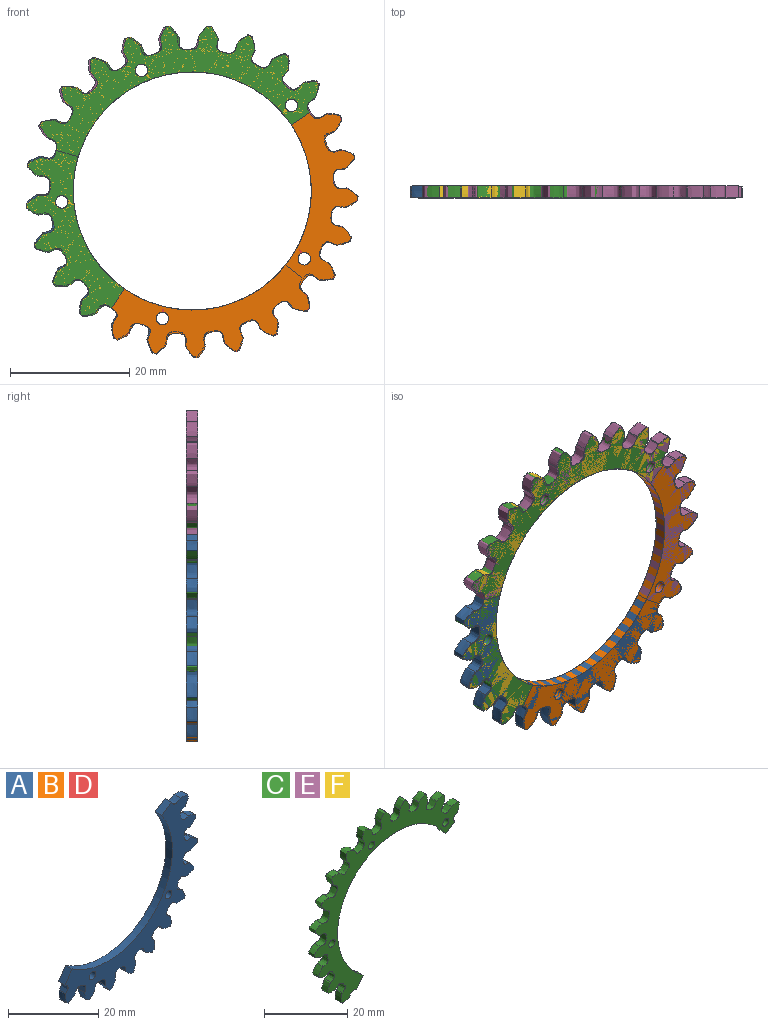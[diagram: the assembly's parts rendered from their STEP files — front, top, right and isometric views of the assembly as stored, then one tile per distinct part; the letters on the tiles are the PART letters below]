
ASSEMBLY  parts=6 mates=5
PART A: 31 faces, bbox 41.5x2x41.2 mm
  f0: extruded ~2x0.02mm, area 0mm2, adj f1,f27,f29,f30
  f1: extruded ~2.79x2mm, area 6.8mm2, adj f0,f2,f29,f30
  f2: plane 3.07x2.05mm, normal (-0.56,0,0.83), area 7.4mm2, adj f1,f3,f29,f30
  f3: cylinder r=20mm len=31.37mm, axis (0,1,0), area 110.6mm2, adj f2,f4,f29,f30
  f4: plane 3.23x2.23mm, normal (-0.82,0,0.57), area 7.9mm2, adj f3,f5,f29,f30
  f5: extruded ~2.53x2mm, area 6.3mm2, adj f4,f6,f29,f30
  f6: extruded ~2.85x2.84mm, area 10.9mm2, adj f5,f7,f29,f30
  f7: extruded ~3.52x2.53mm, area 12.6mm2, adj f6,f8,f29,f30
  f8: extruded ~3.14x2.57mm, area 10.9mm2, adj f7,f9,f29,f30
  f9: extruded ~3.29x2mm, area 12mm2, adj f8,f10,f29,f30
  f10: extruded ~3.25x2.18mm, area 11.1mm2, adj f9,f11,f29,f30
  f11: extruded ~3.31x2.47mm, area 12.7mm2, adj f10,f12,f29,f30
  f12: extruded ~3.18x2.35mm, area 10.9mm2, adj f11,f13,f29,f30
  f13: extruded ~2x0.19mm, area 0.4mm2, adj f12,f14,f29,f30
  f14: extruded ~6.33x2.71mm, area 23.4mm2, adj f13,f15,f29,f30
  f15: extruded ~2x0.18mm, area 0.4mm2, adj f14,f16,f29,f30
  f16: extruded ~6.2x4.09mm, area 23.3mm2, adj f15,f17,f29,f30
  f17: extruded ~2x0.14mm, area 0.4mm2, adj f16,f18,f29,f30
  f18: extruded ~5.84x5.23mm, area 22.7mm2, adj f17,f19,f29,f30
  f19: extruded ~2x0.12mm, area 0.3mm2, adj f18,f20,f29,f30
  f20: extruded ~6.05x5.29mm, area 23.7mm2, adj f19,f21,f29,f30
  f21: extruded ~2x0.09mm, area 0.2mm2, adj f20,f22,f29,f30
  f22: extruded ~6.46x4.47mm, area 24mm2, adj f21,f23,f29,f30
  f23: extruded ~2x0.09mm, area 0.2mm2, adj f22,f24,f29,f30
  f24: extruded ~6.48x3.62mm, area 24mm2, adj f23,f25,f29,f30
  f25: extruded ~2x0.05mm, area 0.1mm2, adj f24,f27,f29,f30
  f26: cylinder r=1.05mm len=2.1mm, axis (0,1,0), area 13.2mm2, adj f29,f30
  f27: extruded ~6.36x2.72mm, area 23.1mm2, adj f0,f25,f29,f30
  f28: cylinder r=1.05mm len=2.1mm, axis (0,1,0), area 13.2mm2, adj f29,f30
  f29: plane 41.46x41.23mm, normal (0,-1,0), area 351.7mm2, adj f0,f1,f2,f3,f4,f5,f6,f7
  f30: plane 41.46x41.23mm, normal (0,1,0), area 351.7mm2, adj f0,f1,f2,f3,f4,f5,f6,f7
PART B: same geometry as A
PART C: 40 faces, bbox 49.2x2x48.9 mm
  f0: extruded ~3.23x2.17mm, area 10.9mm2, adj f1,f36,f38,f39
  f1: extruded ~3.3x2.17mm, area 13mm2, adj f0,f2,f38,f39
  f2: extruded ~3.23x2.1mm, area 10.9mm2, adj f1,f3,f38,f39
  f3: extruded ~3.36x2.72mm, area 12.8mm2, adj f2,f4,f38,f39
  f4: extruded ~3.06x2.51mm, area 10.9mm2, adj f3,f5,f38,f39
  f5: extruded ~3.39x3.1mm, area 12.9mm2, adj f4,f6,f38,f39
  f6: extruded ~2.85x2.68mm, area 10.9mm2, adj f5,f7,f38,f39
  f7: extruded ~3.4x3.29mm, area 13mm2, adj f6,f8,f38,f39
  f8: extruded ~2.8x2.72mm, area 10.8mm2, adj f7,f9,f38,f39
  f9: extruded ~3.41x2.91mm, area 12.4mm2, adj f8,f10,f38,f39
  f10: extruded ~2.98x2.64mm, area 10.9mm2, adj f9,f11,f38,f39
  f11: extruded ~3.73x2.52mm, area 12.7mm2, adj f10,f12,f38,f39
  f12: extruded ~3.19x2.37mm, area 10.9mm2, adj f11,f13,f38,f39
  f13: extruded ~3.29x2.1mm, area 12.7mm2, adj f12,f14,f38,f39
  f14: extruded ~3.25x2.05mm, area 10.9mm2, adj f13,f15,f38,f39
  f15: extruded ~3.33x2.6mm, area 12.7mm2, adj f14,f16,f38,f39
  f16: extruded ~3.13x2.43mm, area 10.9mm2, adj f15,f17,f38,f39
  f17: extruded ~3.29x2.87mm, area 12mm2, adj f16,f18,f38,f39
  f18: extruded ~2.97x2.67mm, area 11.1mm2, adj f17,f19,f38,f39
  f19: extruded ~3.34x3.22mm, area 12.7mm2, adj f18,f20,f38,f39
  f20: extruded ~2.94x2.72mm, area 10.9mm2, adj f19,f21,f38,f39
  f21: extruded ~2.53x2mm, area 6.4mm2, adj f20,f22,f38,f39
  f22: plane 3.23x2.23mm, normal (0.82,0,-0.57), area 7.9mm2, adj f21,f23,f38,f39
  f23: cylinder r=20mm len=36.63mm, axis (0,1,0), area 140.7mm2, adj f22,f24,f38,f39
  f24: plane 3.07x2.05mm, normal (0.56,0,-0.83), area 7.4mm2, adj f23,f25,f38,f39
  f25: extruded ~2.47x2mm, area 6.4mm2, adj f24,f26,f38,f39
  f26: extruded ~2.73x2.7mm, area 10.6mm2, adj f25,f27,f38,f39
  f27: plane 2x0.01mm, normal (-0.37,0,0.93), area 0mm2, adj f26,f28,f38,f39
  f28: extruded ~3.44x3.34mm, area 13.2mm2, adj f27,f29,f38,f39
  f29: extruded ~2.74x2.68mm, area 10.6mm2, adj f28,f30,f38,f39
  f30: plane 2x0.01mm, normal (-0.84,0,0.54), area 0mm2, adj f29,f31,f38,f39
  f31: extruded ~3.53x3.02mm, area 13.2mm2, adj f30,f32,f38,f39
  f32: extruded ~3x2.48mm, area 10.6mm2, adj f31,f33,f38,f39
  f33: plane 2x0.01mm, normal (-0.97,0,0.25), area 0mm2, adj f32,f36,f38,f39
  f34: cylinder r=1.05mm len=2.1mm, axis (0,1,0), area 13.2mm2, adj f38,f39
  f35: cylinder r=1.05mm len=2.1mm, axis (0,1,0), area 13.2mm2, adj f38,f39
  f36: extruded ~3.38x2.41mm, area 12.5mm2, adj f0,f33,f38,f39
  f37: cylinder r=1.05mm len=2.1mm, axis (0,1,0), area 13.2mm2, adj f38,f39
  f38: plane 49.16x48.88mm, normal (0,-1,0), area 441.8mm2, adj f0,f1,f2,f3,f4,f5,f6,f7
  f39: plane 49.16x48.88mm, normal (0,1,0), area 441.8mm2, adj f0,f1,f2,f3,f4,f5,f6,f7
PART D: same geometry as A
PART E: same geometry as C
PART F: same geometry as C
PLACE A rot(axis=(0,1,0),72deg) t=(156.72,12.3,245.83)mm
PLACE B t=(-89.28,12.3,-18.01)mm
PLACE C t=(58.67,12.3,-3.95)mm
PLACE D t=(-89.28,12.3,-18.01)mm
PLACE E rot(axis=(0,1,0),72deg) t=(215.81,12.3,109.47)mm
PLACE F t=(58.67,12.3,-3.95)mm
MATE cylindrical E.f23 <-> F.f23  axis (0,-1,0) through (215.29,10.3,-55.38)mm
MATE fastened C.f24 <-> B.f2  axis (0.56,0,-0.83) through (233.46,11.3,-43.25)mm
MATE fastened F.f24 <-> D.f2  axis (0.56,0,-0.83) through (233.46,11.3,-43.25)mm
MATE fastened E.f24 <-> A.f2  axis (-0.62,0,-0.79) through (232.45,11.3,-68.91)mm
MATE cylindrical C.f23 <-> F.f23  axis (0,-1,0) through (215.29,10.3,-55.38)mm
